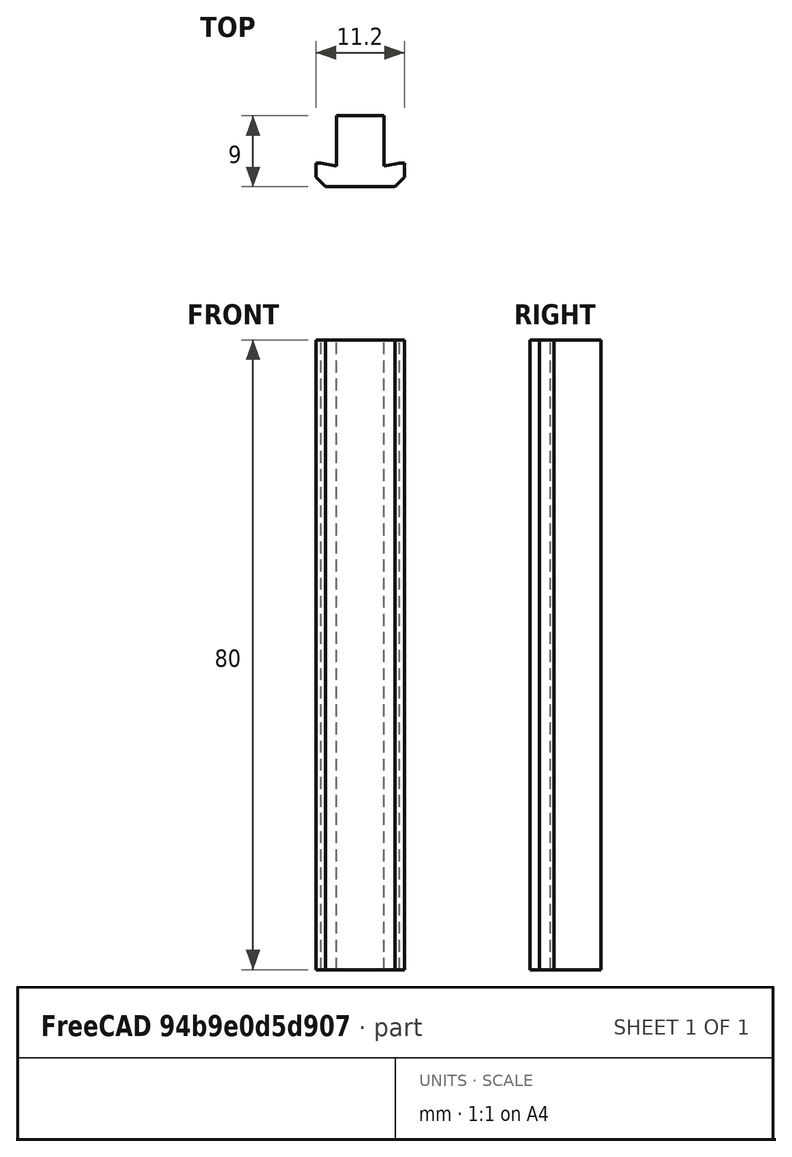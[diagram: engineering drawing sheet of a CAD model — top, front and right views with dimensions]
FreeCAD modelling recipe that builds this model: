
FCSTD DOCUMENT  (FreeCAD 0.19R17798 (Git))
Label: ts4_sub2
License: All rights reserved
LicenseURL: http://en.wikipedia.org/wiki/All_rights_reserved
objects: Sketcher::SketchObject×1, PartDesign::Pad×1, PartDesign::Body×1
note: 4 computed .brp shape members not serialized (recipe doc carries the construction recipe); baked Part::Feature solids carry a one-line shape summary decoded from their .brp

FEATURE [Sketcher::SketchObject] Sketch
  MapMode = 5
  Support = -> [XY_Plane]
  sketch-geometry (12):
    g0: LineSegment StartX=0 StartY=3 StartZ=0 EndX=0 EndY=1.2 EndZ=0
    g1: LineSegment StartX=0 StartY=1.2 StartZ=0 EndX=1.2 EndY=0 EndZ=0
    g2: LineSegment StartX=1.2 StartY=0 StartZ=0 EndX=10 EndY=0 EndZ=0
    g3: LineSegment StartX=10 StartY=0 StartZ=0 EndX=11.2 EndY=1.2 EndZ=0
    g4: LineSegment StartX=11.2 StartY=1.2 StartZ=0 EndX=11.2 EndY=3 EndZ=0
    g5: LineSegment StartX=11.2 StartY=3 StartZ=0 EndX=10.6 EndY=3 EndZ=0
    g6: LineSegment StartX=10.6 StartY=3 StartZ=0 EndX=8.6 EndY=2.6 EndZ=0
    g7: LineSegment StartX=8.6 StartY=2.6 StartZ=0 EndX=8.6 EndY=9 EndZ=0
    g8: LineSegment StartX=8.6 StartY=9 StartZ=0 EndX=2.6 EndY=9 EndZ=0
    g9: LineSegment StartX=2.6 StartY=9 StartZ=0 EndX=2.6 EndY=2.6 EndZ=0
    g10: LineSegment StartX=2.6 StartY=2.6 StartZ=0 EndX=0.6 EndY=3 EndZ=0
    g11: LineSegment StartX=0.6 StartY=3 StartZ=0 EndX=0 EndY=3 EndZ=0
  constraints (36):
    c: Coincident(g0,g1)
    c: Coincident(g1,g2)
    c: Coincident(g2,g3)
    c: Coincident(g3,g4)
    c: Coincident(g4,g5)
    c: Coincident(g5,g6)
    c: Coincident(g6,g7)
    c: Coincident(g7,g8)
    c: Coincident(g8,g9)
    c: Coincident(g9,g10)
    c: Coincident(g10,g11)
    c: Coincident(g11,g0)
    c: DistanceX(g-1,g4) = 11.2
    c: DistanceX(g-1,g8) = 2.6
    c: DistanceX(g8,g8) = 6
    c: DistanceX(g0,g10) = 0.6
    c: DistanceX(g-1,g0) = 0
    c: DistanceX(g0,g-1) = 0
    c: DistanceX(g8,g9) = 0
    c: DistanceY(g-1,g0) = 3
    c: DistanceY(g0,g10) = 0
    c: DistanceY(g-1,g0) = 1.2
    c: DistanceX(g-1,g1) = 1.2
    c: DistanceY(g-1,g9) = 2.6
    c: DistanceY(g9,g8) = 6.4
    c: Horizontal(g8)
    c: DistanceX(g6,g7) = 0
    c: DistanceY(g9,g6) = 0
    c: DistanceX(g5,g4) = 0.6
    c: DistanceY(g0,g4) = 0
    c: DistanceY(g4,g5) = 0
    c: DistanceX(g4,g3) = 0
    c: DistanceY(g-1,g1) = 0
    c: DistanceY(g1,g2) = 0
    c: DistanceY(g2,g3) = 1.2
    c: DistanceX(g2,g3) = 1.2
FEATURE [PartDesign::Pad] Pad
  Length = 80
  Length2 = 100
  Profile = -> Sketch
  Type = 0
FEATURE [PartDesign::Body] Body
  Group = -> [Sketch,Pad]
  Origin = -> Origin
  Tip = -> Pad
